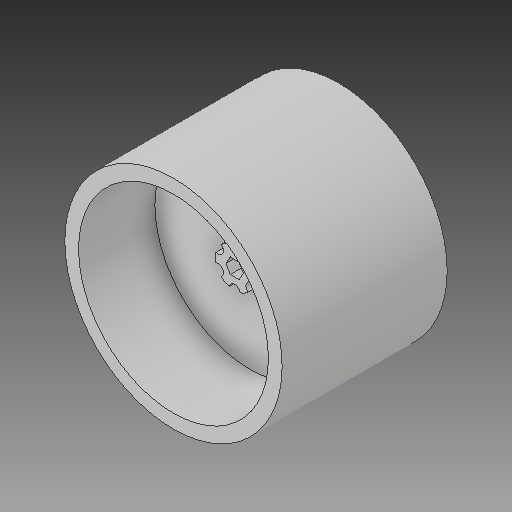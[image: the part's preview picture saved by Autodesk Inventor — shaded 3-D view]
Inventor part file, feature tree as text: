
AUTODESK INVENTOR PART (.ipt)
format: ipt  version: 2019 (Build 230136000, 136)  size: 170,496 bytes
history: native  units: in
note: dims shown in document units (in); Inventor stores cm internally (conversion verified against a paired STEP export)
features: extrude x5, sketch x5
ambient origin geometry x8: Origin, YZ Plane, XZ Plane, XY Plane, X Axis, Y Axis, Z Axis, Center Point
bodies: Solid1 (feature_tree)
feature tree (10):
  extrude  "Extrusion1"  Depth=3.0in TaperAngle=0.0deg
  extrude  "Extrusion2"  Depth=1.2in TaperAngle=0.0deg
  extrude  "Extrusion3"  Depth=0.225in
  extrude  "Extrusion4"  Depth=2.3622in TaperAngle=360.0deg
  extrude  "Extrusion5"  Depth=0.275in
  sketch  "Sketch1"  dims[d0=3.95in d1=3.0in d2=0.0in]
  sketch  "Sketch2"  dims[d3=3.45in d4=1.2in d5=0.0in]
  sketch  "Sketch3"  dims[d6=0.225in d7=0.0in d8=0.7in]
  sketch  "Sketch4"  dims[d10=0.2in d11=2.3622in d13=360.0deg]
  sketch  "Sketch5"  dims[d15=0.275in d16=0.0in d17=0.275in d18=0.225in d19=0.0in]
